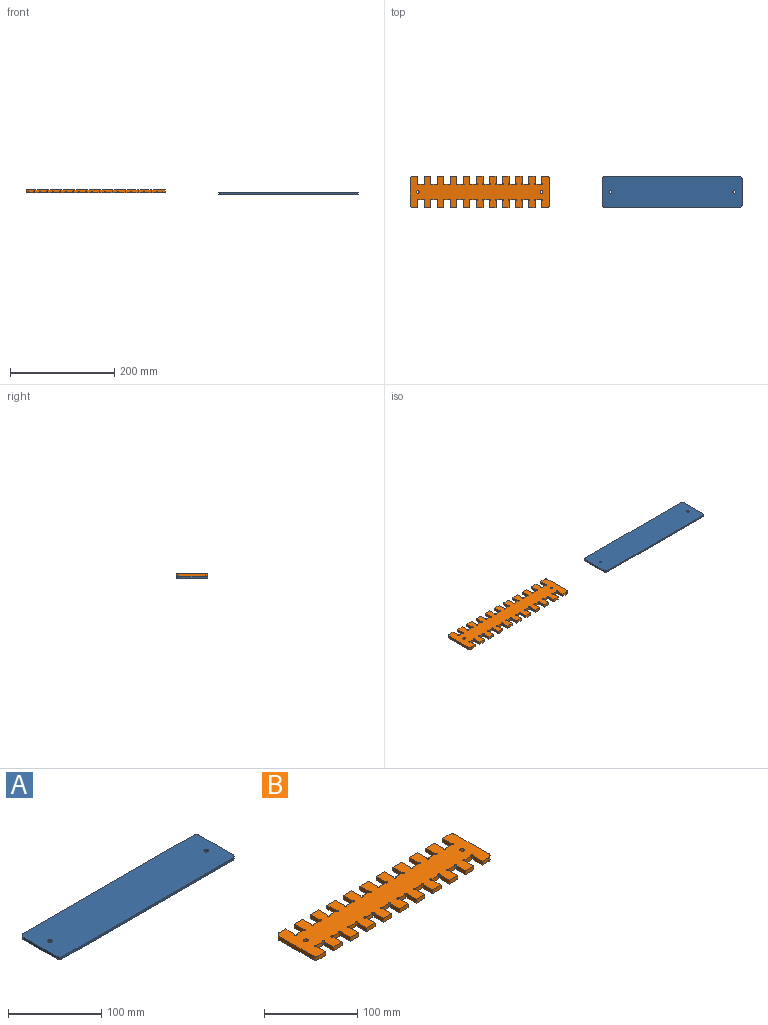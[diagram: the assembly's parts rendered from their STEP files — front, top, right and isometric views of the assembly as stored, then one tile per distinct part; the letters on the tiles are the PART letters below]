
ASSEMBLY  parts=2 mates=1
PART A: 12 faces, bbox 267.2x60x3 mm
  f0: plane 257.2x3mm, normal (0,1,0), area 771.6mm2, adj f1,f9,f10,f11
  f1: cylinder r=5mm len=5mm, axis (0,0,-1), area 23.6mm2, adj f0,f2,f10,f11
  f2: plane 50x3mm, normal (-1,0,0), area 150mm2, adj f1,f3,f10,f11
  f3: cylinder r=5mm len=5mm, axis (0,0,-1), area 23.6mm2, adj f2,f4,f10,f11
  f4: plane 257.2x3mm, normal (0,-1,0), area 771.6mm2, adj f3,f5,f10,f11
  f5: cylinder r=5mm len=5mm, axis (0,0,-1), area 23.6mm2, adj f4,f6,f10,f11
  f6: plane 50x3mm, normal (1,0,0), area 150mm2, adj f5,f9,f10,f11
  f7: cylinder r=2.5mm len=5mm, axis (0,0,-1), area 47.1mm2, adj f10,f11
  f8: cylinder r=2.5mm len=5mm, axis (0,0,-1), area 47.1mm2, adj f10,f11
  f9: cylinder r=5mm len=5mm, axis (0,0,-1), area 23.6mm2, adj f0,f6,f10,f11
  f10: plane 267.2x60mm, normal (0,0,1), area 15971.3mm2, adj f0,f1,f2,f3,f4,f5,f6,f7
  f11: plane 267.2x60mm, normal (0,0,-1), area 15971.3mm2, adj f0,f1,f2,f3,f4,f5,f6,f7
PART B: 132 faces, bbox 267.2x60x5 mm
  f0: plane 13.67x5mm, normal (-1,0,0), area 68.4mm2, adj f1,f129,f130,f131
  f1: cylinder r=1.33mm len=5mm, axis (0,0,1), area 31.3mm2, adj f0,f2,f130,f131
  f2: plane 9.54x5mm, normal (0,-1,0), area 47.7mm2, adj f1,f3,f130,f131
  f3: cylinder r=1.34mm len=5mm, axis (0,0,1), area 31.5mm2, adj f2,f4,f130,f131
  f4: plane 13.66x5mm, normal (1,0,0), area 68.3mm2, adj f3,f5,f130,f131
  f5: plane 12.8x5mm, normal (0,-1,0), area 64mm2, adj f4,f6,f130,f131
  f6: plane 13.67x5mm, normal (-1,0,0), area 68.4mm2, adj f5,f7,f130,f131
  f7: cylinder r=1.33mm len=5mm, axis (0,0,1), area 31.3mm2, adj f6,f8,f130,f131
  f8: plane 9.54x5mm, normal (0,-1,0), area 47.7mm2, adj f7,f9,f130,f131
  f9: cylinder r=1.34mm len=5mm, axis (0,0,1), area 31.5mm2, adj f8,f10,f130,f131
  f10: plane 13.66x5mm, normal (1,0,0), area 68.3mm2, adj f9,f11,f130,f131
  f11: plane 12.8x5mm, normal (0,-1,0), area 64mm2, adj f10,f12,f130,f131
  f12: plane 13.67x5mm, normal (-1,0,0), area 68.4mm2, adj f11,f13,f130,f131
  f13: cylinder r=1.33mm len=5mm, axis (0,0,1), area 31.3mm2, adj f12,f14,f130,f131
  f14: plane 9.54x5mm, normal (0,-1,0), area 47.7mm2, adj f13,f15,f130,f131
  f15: cylinder r=1.34mm len=5mm, axis (0,0,1), area 31.5mm2, adj f14,f16,f130,f131
  f16: plane 13.66x5mm, normal (1,0,0), area 68.3mm2, adj f15,f17,f130,f131
  f17: plane 12.8x5mm, normal (0,-1,0), area 64mm2, adj f16,f18,f130,f131
  f18: plane 13.67x5mm, normal (-1,0,0), area 68.4mm2, adj f17,f19,f130,f131
  f19: cylinder r=1.33mm len=5mm, axis (0,0,1), area 31.3mm2, adj f18,f20,f130,f131
  f20: plane 9.54x5mm, normal (0,-1,0), area 47.7mm2, adj f19,f21,f130,f131
  f21: cylinder r=1.34mm len=5mm, axis (0,0,1), area 31.5mm2, adj f20,f22,f130,f131
  f22: plane 13.66x5mm, normal (1,0,0), area 68.3mm2, adj f21,f23,f130,f131
  f23: plane 12.8x5mm, normal (0,-1,0), area 64mm2, adj f22,f24,f130,f131
  f24: plane 13.67x5mm, normal (-1,0,0), area 68.4mm2, adj f23,f25,f130,f131
  f25: cylinder r=1.33mm len=5mm, axis (0,0,1), area 31.3mm2, adj f24,f26,f130,f131
  f26: plane 9.54x5mm, normal (0,-1,0), area 47.7mm2, adj f25,f27,f130,f131
  f27: cylinder r=1.34mm len=5mm, axis (0,0,1), area 31.5mm2, adj f26,f28,f130,f131
  f28: plane 13.66x5mm, normal (1,0,0), area 68.3mm2, adj f27,f29,f130,f131
  f29: plane 12.8x5mm, normal (0,-1,0), area 64mm2, adj f28,f30,f130,f131
  f30: plane 13.67x5mm, normal (-1,0,0), area 68.4mm2, adj f29,f31,f130,f131
  f31: cylinder r=1.33mm len=5mm, axis (0,0,1), area 31.3mm2, adj f30,f32,f130,f131
  f32: plane 9.54x5mm, normal (0,-1,0), area 47.7mm2, adj f31,f33,f130,f131
  f33: cylinder r=1.34mm len=5mm, axis (0,0,1), area 31.5mm2, adj f32,f34,f130,f131
  f34: plane 13.66x5mm, normal (1,0,0), area 68.3mm2, adj f33,f35,f130,f131
  f35: plane 12.8x5mm, normal (0,-1,0), area 64mm2, adj f34,f36,f130,f131
  f36: plane 13.67x5mm, normal (-1,0,0), area 68.4mm2, adj f35,f37,f130,f131
  f37: cylinder r=1.33mm len=5mm, axis (0,0,1), area 31.3mm2, adj f36,f38,f130,f131
  f38: plane 9.54x5mm, normal (0,-1,0), area 47.7mm2, adj f37,f39,f130,f131
  f39: cylinder r=1.34mm len=5mm, axis (0,0,1), area 31.5mm2, adj f38,f40,f130,f131
  f40: plane 13.66x5mm, normal (1,0,0), area 68.3mm2, adj f39,f41,f130,f131
  f41: plane 10x5mm, normal (0,-1,0), area 50mm2, adj f40,f42,f130,f131
  f42: cylinder r=5mm len=5mm, axis (0,0,1), area 39.3mm2, adj f41,f43,f130,f131
  f43: plane 50x5mm, normal (-1,0,0), area 250mm2, adj f42,f44,f130,f131
  f44: cylinder r=5mm len=5mm, axis (0,0,1), area 39.3mm2, adj f43,f45,f130,f131
  f45: plane 10x5mm, normal (0,1,0), area 50mm2, adj f44,f46,f130,f131
  f46: plane 13.66x5mm, normal (1,0,0), area 68.3mm2, adj f45,f47,f130,f131
  f47: cylinder r=1.34mm len=5mm, axis (0,0,1), area 31.5mm2, adj f46,f48,f130,f131
  f48: plane 9.54x5mm, normal (0,1,0), area 47.7mm2, adj f47,f49,f130,f131
  f49: cylinder r=1.33mm len=5mm, axis (0,0,1), area 31.3mm2, adj f48,f50,f130,f131
  f50: plane 13.67x5mm, normal (-1,0,0), area 68.4mm2, adj f49,f51,f130,f131
  f51: plane 12.8x5mm, normal (0,1,0), area 64mm2, adj f50,f52,f130,f131
  f52: plane 13.66x5mm, normal (1,0,0), area 68.3mm2, adj f51,f53,f130,f131
  f53: cylinder r=1.34mm len=5mm, axis (0,0,1), area 31.5mm2, adj f52,f54,f130,f131
  f54: plane 9.54x5mm, normal (0,1,0), area 47.7mm2, adj f53,f55,f130,f131
  f55: cylinder r=1.33mm len=5mm, axis (0,0,1), area 31.3mm2, adj f54,f56,f130,f131
  f56: plane 13.67x5mm, normal (-1,0,0), area 68.4mm2, adj f55,f57,f130,f131
  f57: plane 12.8x5mm, normal (0,1,0), area 64mm2, adj f56,f58,f130,f131
  f58: plane 13.66x5mm, normal (1,0,0), area 68.3mm2, adj f57,f59,f130,f131
  f59: cylinder r=1.34mm len=5mm, axis (0,0,1), area 31.5mm2, adj f58,f60,f130,f131
  f60: plane 9.54x5mm, normal (0,1,0), area 47.7mm2, adj f59,f61,f130,f131
  f61: cylinder r=1.33mm len=5mm, axis (0,0,1), area 31.3mm2, adj f60,f62,f130,f131
  f62: plane 13.67x5mm, normal (-1,0,0), area 68.4mm2, adj f61,f63,f130,f131
  f63: plane 12.8x5mm, normal (0,1,0), area 64mm2, adj f62,f64,f130,f131
  f64: plane 13.66x5mm, normal (1,0,0), area 68.3mm2, adj f63,f65,f130,f131
  f65: cylinder r=1.34mm len=5mm, axis (0,0,1), area 31.5mm2, adj f64,f66,f130,f131
  f66: plane 9.54x5mm, normal (0,1,0), area 47.7mm2, adj f65,f67,f130,f131
  f67: cylinder r=1.33mm len=5mm, axis (0,0,1), area 31.3mm2, adj f66,f68,f130,f131
  f68: plane 13.67x5mm, normal (-1,0,0), area 68.4mm2, adj f67,f69,f130,f131
  f69: plane 12.8x5mm, normal (0,1,0), area 64mm2, adj f68,f70,f130,f131
  f70: plane 13.66x5mm, normal (1,0,0), area 68.3mm2, adj f69,f71,f130,f131
  f71: cylinder r=1.34mm len=5mm, axis (0,0,1), area 31.5mm2, adj f70,f72,f130,f131
  f72: plane 9.54x5mm, normal (0,1,0), area 47.7mm2, adj f71,f73,f130,f131
  f73: cylinder r=1.33mm len=5mm, axis (0,0,1), area 31.3mm2, adj f72,f74,f130,f131
  f74: plane 13.67x5mm, normal (-1,0,0), area 68.4mm2, adj f73,f75,f130,f131
  f75: plane 12.8x5mm, normal (0,1,0), area 64mm2, adj f74,f76,f130,f131
  f76: plane 13.66x5mm, normal (1,0,0), area 68.3mm2, adj f75,f77,f130,f131
  f77: cylinder r=1.34mm len=5mm, axis (0,0,1), area 31.5mm2, adj f76,f78,f130,f131
  f78: plane 9.54x5mm, normal (0,1,0), area 47.7mm2, adj f77,f79,f130,f131
  f79: cylinder r=1.33mm len=5mm, axis (0,0,1), area 31.3mm2, adj f78,f80,f130,f131
  f80: plane 13.67x5mm, normal (-1,0,0), area 68.4mm2, adj f79,f81,f130,f131
  f81: plane 12.8x5mm, normal (0,1,0), area 64mm2, adj f80,f82,f130,f131
  f82: plane 13.66x5mm, normal (1,0,0), area 68.3mm2, adj f81,f83,f130,f131
  f83: cylinder r=1.34mm len=5mm, axis (0,0,1), area 31.5mm2, adj f82,f84,f130,f131
  f84: plane 9.54x5mm, normal (0,1,0), area 47.7mm2, adj f83,f85,f130,f131
  f85: cylinder r=1.33mm len=5mm, axis (0,0,1), area 31.3mm2, adj f84,f86,f130,f131
  f86: plane 13.67x5mm, normal (-1,0,0), area 68.4mm2, adj f85,f87,f130,f131
  f87: plane 12.8x5mm, normal (0,1,0), area 64mm2, adj f86,f88,f130,f131
  f88: plane 13.66x5mm, normal (1,0,0), area 68.3mm2, adj f87,f89,f130,f131
  f89: cylinder r=1.34mm len=5mm, axis (0,0,1), area 31.5mm2, adj f88,f90,f130,f131
  f90: plane 9.54x5mm, normal (0,1,0), area 47.7mm2, adj f89,f91,f130,f131
  f91: cylinder r=1.33mm len=5mm, axis (0,0,1), area 31.3mm2, adj f90,f92,f130,f131
  f92: plane 13.67x5mm, normal (-1,0,0), area 68.4mm2, adj f91,f93,f130,f131
  f93: plane 12.8x5mm, normal (0,1,0), area 64mm2, adj f92,f94,f130,f131
  f94: plane 13.66x5mm, normal (1,0,0), area 68.3mm2, adj f93,f95,f130,f131
  f95: cylinder r=1.34mm len=5mm, axis (0,0,1), area 31.5mm2, adj f94,f96,f130,f131
  f96: plane 9.54x5mm, normal (0,1,0), area 47.7mm2, adj f95,f97,f130,f131
  f97: cylinder r=1.33mm len=5mm, axis (0,0,1), area 31.3mm2, adj f96,f98,f130,f131
  f98: plane 13.67x5mm, normal (-1,0,0), area 68.4mm2, adj f97,f99,f130,f131
  f99: plane 12.8x5mm, normal (0,1,0), area 64mm2, adj f98,f100,f130,f131
  f100: plane 13.66x5mm, normal (1,0,0), area 68.3mm2, adj f99,f101,f130,f131
  f101: cylinder r=1.34mm len=5mm, axis (0,0,1), area 31.5mm2, adj f100,f102,f130,f131
  f102: plane 9.54x5mm, normal (0,1,0), area 47.7mm2, adj f101,f103,f130,f131
  f103: cylinder r=1.33mm len=5mm, axis (0,0,1), area 31.3mm2, adj f102,f104,f130,f131
  f104: plane 13.67x5mm, normal (-1,0,0), area 68.4mm2, adj f103,f105,f130,f131
  f105: plane 10x5mm, normal (0,1,0), area 50mm2, adj f104,f106,f130,f131
  f106: cylinder r=5mm len=5mm, axis (0,0,1), area 39.3mm2, adj f105,f107,f130,f131
  f107: plane 50x5mm, normal (1,0,0), area 250mm2, adj f106,f108,f130,f131
  f108: cylinder r=5mm len=5mm, axis (0,0,1), area 39.3mm2, adj f107,f109,f130,f131
  f109: plane 10x5mm, normal (0,-1,0), area 50mm2, adj f108,f110,f130,f131
  f110: plane 13.67x5mm, normal (-1,0,0), area 68.4mm2, adj f109,f111,f130,f131
  f111: cylinder r=1.33mm len=5mm, axis (0,0,1), area 31.3mm2, adj f110,f112,f130,f131
  f112: plane 9.54x5mm, normal (0,-1,0), area 47.7mm2, adj f111,f113,f130,f131
  f113: cylinder r=1.34mm len=5mm, axis (0,0,1), area 31.5mm2, adj f112,f114,f130,f131
  f114: plane 13.66x5mm, normal (1,0,0), area 68.3mm2, adj f113,f115,f130,f131
  f115: plane 12.8x5mm, normal (0,-1,0), area 64mm2, adj f114,f116,f130,f131
  f116: plane 13.67x5mm, normal (-1,0,0), area 68.4mm2, adj f115,f117,f130,f131
  f117: cylinder r=1.33mm len=5mm, axis (0,0,1), area 31.3mm2, adj f116,f118,f130,f131
  f118: plane 9.54x5mm, normal (0,-1,0), area 47.7mm2, adj f117,f119,f130,f131
  f119: cylinder r=1.34mm len=5mm, axis (0,0,1), area 31.5mm2, adj f118,f120,f130,f131
  f120: plane 13.66x5mm, normal (1,0,0), area 68.3mm2, adj f119,f121,f130,f131
  f121: plane 12.8x5mm, normal (0,-1,0), area 64mm2, adj f120,f122,f130,f131
  f122: plane 13.67x5mm, normal (-1,0,0), area 68.4mm2, adj f121,f123,f130,f131
  f123: cylinder r=1.33mm len=5mm, axis (0,0,1), area 31.3mm2, adj f122,f124,f130,f131
  f124: plane 9.54x5mm, normal (0,-1,0), area 47.7mm2, adj f123,f125,f130,f131
  f125: cylinder r=1.34mm len=5mm, axis (0,0,1), area 31.5mm2, adj f124,f126,f130,f131
  f126: plane 13.66x5mm, normal (1,0,0), area 68.3mm2, adj f125,f129,f130,f131
  f127: cylinder r=2.5mm len=5mm, axis (0,0,1), area 78.5mm2, adj f130,f131
  f128: cylinder r=2.5mm len=5mm, axis (0,0,1), area 78.5mm2, adj f130,f131
  f129: plane 12.8x5mm, normal (0,-1,0), area 64mm2, adj f0,f126,f130,f131
  f130: plane 267.2x60mm, normal (0,0,-1), area 12143.9mm2, adj f0,f1,f2,f3,f4,f5,f6,f7
  f131: plane 267.2x60mm, normal (0,0,1), area 12143.9mm2, adj f0,f1,f2,f3,f4,f5,f6,f7
PLACE A rot(axis=(0,1,0),180deg) t=(140.06,62.34,-3.08)mm
PLACE B t=(-232.27,62.34,-6.08)mm
MATE pin_slot B.f128 <-> A.f8  axis (0,0,-1) through (-349.34,44.45,-3.08)mm
